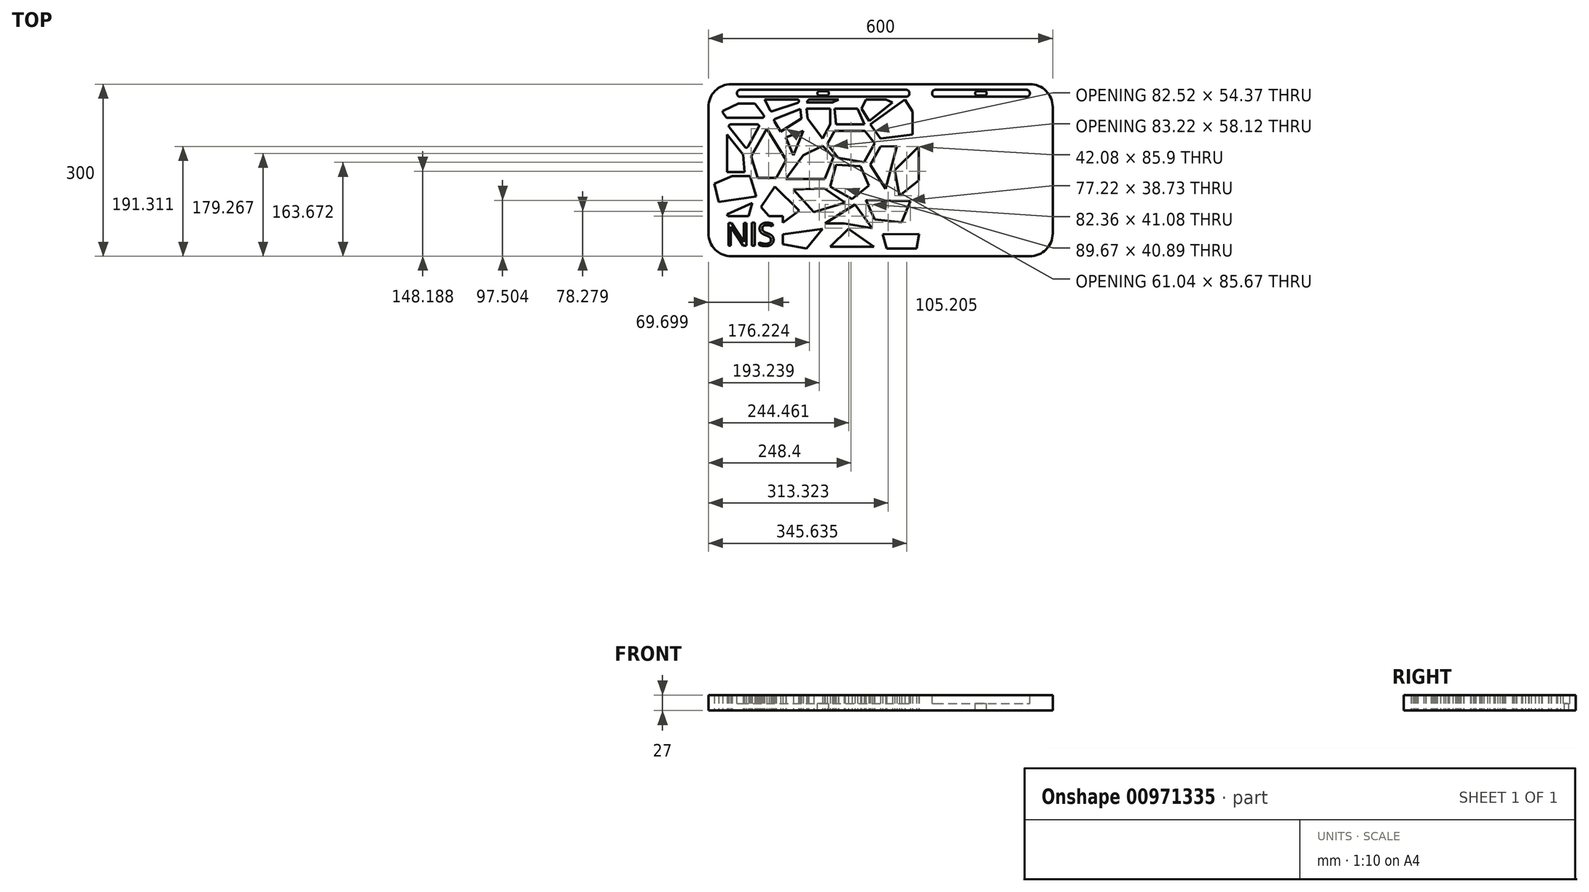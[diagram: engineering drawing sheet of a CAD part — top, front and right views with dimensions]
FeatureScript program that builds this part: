
annotation { "Feature Type Name" : "Feature", "Feature Type Description" : "" }
export const myFeature = defineFeature(function(context is Context, id is Id, definition is map)
    precondition{}
    {
        {
            var Q0;
            Q0=qCreatedBy(makeId("Top.planeOp"),FACE);
            var sketch = newSketch(context, id + "F0", { "sketchPlane" : qUnion([Q0])});
            skLineSegment(sketch, "E0.bottom", {"start": v(260, 150) * mm, "end": v(-260, 150) * mm});
            skLineSegment(sketch, "E0.top", {"start": v(260, -150) * mm, "end": v(-260, -150) * mm});
            skLineSegment(sketch, "E0.left", {"start": v(300, 110) * mm, "end": v(300, -110) * mm});
            skLineSegment(sketch, "E0.right", {"start": v(-300, 110) * mm, "end": v(-300, -110) * mm});
            skPoint(sketch, "E0.middle", {"position": v(0, 0) * mm});
            skPoint(sketch, "E1.visualSharp", {"position": v(-300, 150) * mm});
            skArc(sketch, "E1.filletArc", {"start": v(-260, 150) * mm, "mid": v(-288.28, 138.28) * mm, "end": v(-300, 110) * mm});
            skPoint(sketch, "E2.visualSharp", {"position": v(-300, -150) * mm});
            skArc(sketch, "E2.filletArc", {"start": v(-300, -110) * mm, "mid": v(-288.28, -138.28) * mm, "end": v(-260, -150) * mm});
            skPoint(sketch, "E3.visualSharp", {"position": v(300, -150) * mm});
            skArc(sketch, "E3.filletArc", {"start": v(260, -150) * mm, "mid": v(288.28, -138.28) * mm, "end": v(300, -110) * mm});
            skPoint(sketch, "E4.visualSharp", {"position": v(300, 150) * mm});
            skArc(sketch, "E4.filletArc", {"start": v(300, 110) * mm, "mid": v(288.28, 138.28) * mm, "end": v(260, 150) * mm});
            skLineSegment(sketch, "E5", {"start": v(80, 150) * mm, "end": v(80, -150) * mm, "construction": true});
            skSolve(sketch);
        }
        {
            var Q0;
            Q0=makeQuery(id+"F0.imprint","IMPRINT",FACE,{"disambiguationData":[TD([[makeQuery(id+"F0.imprint","IMPRINT",EDGE,{"derivedFrom":sQuery(id+"F0.wireOp",EDGE,"E0.bottom")}),1.0]])]});
            var sketch = newSketch(context, id + "F1", { "sketchPlane" : qUnion([Q0])});
            skLineSegment(sketch, "E6", {"start": v(-273.2, 104.35) * mm, "end": v(-247.8, 116.08) * mm});
            skLineSegment(sketch, "E7", {"start": v(-246.54, 116.36) * mm, "end": v(-221.1, 116.36) * mm});
            skLineSegment(sketch, "E8", {"start": v(-218.74, 115.22) * mm, "end": v(-203.73, 96.16) * mm});
            skLineSegment(sketch, "E9", {"start": v(-206.09, 91.3) * mm, "end": v(-266.95, 91.3) * mm});
            skLineSegment(sketch, "E10", {"start": v(-269.43, 92.61) * mm, "end": v(-274.42, 99.94) * mm});
            skLineSegment(sketch, "E11", {"start": v(-184.96, 85.23) * mm, "end": v(-173.85, 67.5) * mm});
            skLineSegment(sketch, "E12", {"start": v(-173.85, 67.5) * mm, "end": v(-137.63, 90.2) * mm});
            skLineSegment(sketch, "E13", {"start": v(-137.63, 90.2) * mm, "end": v(-140.04, 106.58) * mm});
            skLineSegment(sketch, "E14", {"start": v(-140.04, 106.58) * mm, "end": v(-183.5, 89.61) * mm});
            skLineSegment(sketch, "E15", {"start": v(-202.21, 122.97) * mm, "end": v(-192.5, 104.48) * mm});
            skLineSegment(sketch, "E16", {"start": v(-188.92, 103.02) * mm, "end": v(-144.36, 117.51) * mm});
            skLineSegment(sketch, "E17", {"start": v(-142.34, 120.89) * mm, "end": v(-142.7, 122.97) * mm});
            skLineSegment(sketch, "E18", {"start": v(-129.26, 107.06) * mm, "end": v(-126.94, 90) * mm});
            skLineSegment(sketch, "E19", {"start": v(-126.94, 90) * mm, "end": v(-101.24, 55.24) * mm});
            skLineSegment(sketch, "E20", {"start": v(-101.24, 55.24) * mm, "end": v(-87.55, 79.67) * mm});
            skLineSegment(sketch, "E21", {"start": v(-87.55, 79.67) * mm, "end": v(-87.55, 107.48) * mm});
            skLineSegment(sketch, "E22", {"start": v(-87.55, 107.48) * mm, "end": v(-129.26, 107.06) * mm});
            skLineSegment(sketch, "E23", {"start": v(-79.98, 107.06) * mm, "end": v(-77.5, 79.67) * mm});
            skLineSegment(sketch, "E24", {"start": v(-77.5, 79.67) * mm, "end": v(-27.9, 79.67) * mm});
            skLineSegment(sketch, "E25", {"start": v(-27.9, 79.67) * mm, "end": v(-39.95, 107.06) * mm});
            skLineSegment(sketch, "E26", {"start": v(-39.95, 107.06) * mm, "end": v(-79.98, 107.06) * mm});
            skLineSegment(sketch, "E27", {"start": v(-263.7, 74.8) * mm, "end": v(-236.4, 40.48) * mm});
            skLineSegment(sketch, "E28", {"start": v(-231.43, 40.88) * mm, "end": v(-212.2, 75.2) * mm});
            skLineSegment(sketch, "E29", {"start": v(-214.81, 79.67) * mm, "end": v(-261.36, 79.67) * mm});
            skLineSegment(sketch, "E30", {"start": v(-198.5, 72.1) * mm, "end": v(-225.31, 24.27) * mm});
            skLineSegment(sketch, "E31", {"start": v(-225.31, 24.27) * mm, "end": v(-214.04, -13.57) * mm});
            skLineSegment(sketch, "E32", {"start": v(-214.04, -13.57) * mm, "end": v(-181.98, -13.57) * mm});
            skLineSegment(sketch, "E33", {"start": v(-181.98, -13.57) * mm, "end": v(-164.28, 18.02) * mm});
            skLineSegment(sketch, "E34", {"start": v(-164.28, 18.02) * mm, "end": v(-198.5, 72.1) * mm});
            skLineSegment(sketch, "E35", {"start": v(-165.39, 56.97) * mm, "end": v(-151.83, 26.15) * mm});
            skLineSegment(sketch, "E36", {"start": v(-151.83, 26.15) * mm, "end": v(-134.83, 68.5) * mm});
            skLineSegment(sketch, "E37", {"start": v(-134.83, 68.5) * mm, "end": v(-165.39, 56.97) * mm});
            skLineSegment(sketch, "E38", {"start": v(-267.58, 62.27) * mm, "end": v(-239.65, 27.15) * mm});
            skLineSegment(sketch, "E39", {"start": v(-239.65, 27.15) * mm, "end": v(-236.87, -3.55) * mm});
            skLineSegment(sketch, "E40", {"start": v(-236.87, -3.55) * mm, "end": v(-267.58, -3.55) * mm});
            skLineSegment(sketch, "E41", {"start": v(-267.58, -3.55) * mm, "end": v(-267.58, 62.27) * mm});
            skLineSegment(sketch, "E42", {"start": v(-134.83, 26.2) * mm, "end": v(-165.39, -15.39) * mm});
            skLineSegment(sketch, "E43", {"start": v(-165.39, -15.39) * mm, "end": v(-97.55, -15.39) * mm});
            skLineSegment(sketch, "E44", {"start": v(-97.55, -15.39) * mm, "end": v(-82.16, 22.94) * mm});
            skLineSegment(sketch, "E45", {"start": v(-82.16, 22.94) * mm, "end": v(-101.24, 42.73) * mm});
            skLineSegment(sketch, "E46", {"start": v(-101.24, 42.73) * mm, "end": v(-134.83, 26.2) * mm});
            skLineSegment(sketch, "E47", {"start": v(-129.26, 118.32) * mm, "end": v(-83.9, 118.32) * mm});
            skLineSegment(sketch, "E48", {"start": v(-83.9, 118.32) * mm, "end": v(-73.33, 122.97) * mm});
            skLineSegment(sketch, "E49", {"start": v(-33.3, 107.06) * mm, "end": v(-19.85, 85.83) * mm});
            skLineSegment(sketch, "E50", {"start": v(-19.85, 85.83) * mm, "end": v(21, 118.32) * mm});
            skLineSegment(sketch, "E51", {"start": v(21, 118.32) * mm, "end": v(9.4, 122.97) * mm});
            skLineSegment(sketch, "E52", {"start": v(-25.38, 122.97) * mm, "end": v(-33.3, 107.06) * mm});
            skLineSegment(sketch, "E53", {"start": v(42.52, 123.2) * mm, "end": v(55.79, 102.24) * mm});
            skLineSegment(sketch, "E54", {"start": v(55.79, 102.24) * mm, "end": v(55.79, 62.27) * mm});
            skLineSegment(sketch, "E55", {"start": v(55.79, 62.27) * mm, "end": v(0, 55.24) * mm});
            skLineSegment(sketch, "E56", {"start": v(0, 55.24) * mm, "end": v(-18.07, 79.67) * mm});
            skLineSegment(sketch, "E57", {"start": v(-18.07, 79.67) * mm, "end": v(42.52, 123.2) * mm});
            skLineSegment(sketch, "E58", {"start": v(-79.98, 68.5) * mm, "end": v(-92.86, 45.51) * mm});
            skLineSegment(sketch, "E59", {"start": v(-92.86, 45.51) * mm, "end": v(-73.99, 21.8) * mm});
            skLineSegment(sketch, "E60", {"start": v(-73.99, 21.8) * mm, "end": v(-28.83, 14.13) * mm});
            skLineSegment(sketch, "E61", {"start": v(-28.83, 14.13) * mm, "end": v(-10.34, 47.12) * mm});
            skLineSegment(sketch, "E62", {"start": v(-10.34, 47.12) * mm, "end": v(-27.34, 68.5) * mm});
            skLineSegment(sketch, "E63", {"start": v(-27.34, 68.5) * mm, "end": v(-79.98, 68.5) * mm});
            skLineSegment(sketch, "E64", {"start": v(-77.5, 9.58) * mm, "end": v(-87.55, -28.5) * mm});
            skLineSegment(sketch, "E65", {"start": v(-87.55, -28.5) * mm, "end": v(-49.32, -49.92) * mm});
            skLineSegment(sketch, "E66", {"start": v(-49.32, -49.92) * mm, "end": v(-20.2, -26.75) * mm});
            skLineSegment(sketch, "E67", {"start": v(-20.2, -26.75) * mm, "end": v(-35.07, 7.05) * mm});
            skLineSegment(sketch, "E68", {"start": v(-35.07, 7.05) * mm, "end": v(-77.5, 9.58) * mm});
            skLineSegment(sketch, "E69", {"start": v(0, 41.14) * mm, "end": v(-17.69, 9.58) * mm});
            skLineSegment(sketch, "E70", {"start": v(-17.69, 9.58) * mm, "end": v(8.76, -32.2) * mm});
            skLineSegment(sketch, "E71", {"start": v(8.76, -32.2) * mm, "end": v(28.33, 41.95) * mm});
            skLineSegment(sketch, "E72", {"start": v(28.33, 41.95) * mm, "end": v(0, 41.14) * mm});
            skLineSegment(sketch, "E73", {"start": v(24.6, 0) * mm, "end": v(66.68, 41.14) * mm});
            skLineSegment(sketch, "E74", {"start": v(66.68, 41.14) * mm, "end": v(66.68, -17.98) * mm});
            skLineSegment(sketch, "E75", {"start": v(66.68, -17.98) * mm, "end": v(33, -44.76) * mm});
            skLineSegment(sketch, "E76", {"start": v(33, -44.76) * mm, "end": v(24.6, 0) * mm});
            skLineSegment(sketch, "E77", {"start": v(-289.54, -23.85) * mm, "end": v(-258.24, -10.08) * mm});
            skLineSegment(sketch, "E78", {"start": v(-258.24, -10.08) * mm, "end": v(-227.41, -10.08) * mm});
            skLineSegment(sketch, "E79", {"start": v(-227.41, -10.08) * mm, "end": v(-216.84, -45.58) * mm});
            skLineSegment(sketch, "E80", {"start": v(-216.84, -45.58) * mm, "end": v(-282.02, -55.41) * mm});
            skLineSegment(sketch, "E81", {"start": v(-282.02, -55.41) * mm, "end": v(-289.54, -23.85) * mm});
            skLineSegment(sketch, "E82", {"start": v(-184.06, -28.5) * mm, "end": v(-208.5, -64.27) * mm});
            skLineSegment(sketch, "E83", {"start": v(-208.5, -64.27) * mm, "end": v(-194.3, -80) * mm});
            skLineSegment(sketch, "E84", {"start": v(-170, -91.42) * mm, "end": v(-141.88, -70.63) * mm});
            skLineSegment(sketch, "E85", {"start": v(-141.88, -70.63) * mm, "end": v(-184.06, -28.5) * mm});
            skLineSegment(sketch, "E86", {"start": v(-151.6, -33.6) * mm, "end": v(-97.67, -32.05) * mm});
            skLineSegment(sketch, "E87", {"start": v(-97.67, -32.05) * mm, "end": v(-61.93, -56.83) * mm});
            skLineSegment(sketch, "E88", {"start": v(-61.93, -56.83) * mm, "end": v(-116.02, -72.94) * mm});
            skLineSegment(sketch, "E89", {"start": v(-116.02, -72.94) * mm, "end": v(-151.6, -33.6) * mm});
            skLineSegment(sketch, "E90", {"start": v(-25.29, -52.36) * mm, "end": v(-10.53, -85.91) * mm});
            skLineSegment(sketch, "E91", {"start": v(-10.53, -85.91) * mm, "end": v(36.97, -91.08) * mm});
            skLineSegment(sketch, "E92", {"start": v(36.97, -91.08) * mm, "end": v(51.93, -53.82) * mm});
            skLineSegment(sketch, "E93", {"start": v(51.93, -53.82) * mm, "end": v(-25.29, -52.36) * mm});
            skLineSegment(sketch, "E94", {"start": v(-267.58, -76.66) * mm, "end": v(-223.88, -57.44) * mm});
            skLineSegment(sketch, "E95", {"start": v(-223.88, -57.44) * mm, "end": v(-229.83, -80) * mm});
            skLineSegment(sketch, "E96", {"start": v(-265.98, -80) * mm, "end": v(-267.58, -76.66) * mm});
            skLineSegment(sketch, "E97", {"start": v(-170, -128.9) * mm, "end": v(-129.26, -136.9) * mm});
            skLineSegment(sketch, "E98", {"start": v(-129.26, -136.9) * mm, "end": v(-101.24, -102.36) * mm});
            skLineSegment(sketch, "E99", {"start": v(-101.24, -102.36) * mm, "end": v(-170, -111.76) * mm});
            skLineSegment(sketch, "E100", {"start": v(-63.44, -92.67) * mm, "end": v(-96.72, -92.67) * mm});
            skLineSegment(sketch, "E101", {"start": v(-96.72, -92.67) * mm, "end": v(-44.74, -59.76) * mm});
            skLineSegment(sketch, "E102", {"start": v(-44.74, -59.76) * mm, "end": v(-14.36, -100.84) * mm});
            skLineSegment(sketch, "E103", {"start": v(-14.36, -100.84) * mm, "end": v(-63.44, -92.67) * mm});
            skLineSegment(sketch, "E104", {"start": v(-87.55, -133.1) * mm, "end": v(-11.62, -133.1) * mm});
            skLineSegment(sketch, "E105", {"start": v(-11.62, -133.1) * mm, "end": v(-56.1, -102.28) * mm});
            skLineSegment(sketch, "E106", {"start": v(-56.1, -102.28) * mm, "end": v(-87.55, -133.1) * mm});
            skLineSegment(sketch, "E107", {"start": v(3.55, -112.05) * mm, "end": v(10.78, -136.33) * mm});
            skLineSegment(sketch, "E108", {"start": v(10.78, -136.33) * mm, "end": v(62.52, -136.33) * mm});
            skLineSegment(sketch, "E109", {"start": v(62.52, -136.33) * mm, "end": v(67.47, -111.19) * mm});
            skLineSegment(sketch, "E110", {"start": v(67.47, -111.19) * mm, "end": v(3.55, -112.05) * mm});
            skPoint(sketch, "E111.visualSharp", {"position": v(-276.4, 102.86) * mm});
            skArc(sketch, "E111.filletArc", {"start": v(-273.2, 104.35) * mm, "mid": v(-274.83, 102.42) * mm, "end": v(-274.42, 99.94) * mm});
            skPoint(sketch, "E112.visualSharp", {"position": v(-268.54, 91.3) * mm});
            skArc(sketch, "E112.filletArc", {"start": v(-269.43, 92.61) * mm, "mid": v(-268.36, 91.65) * mm, "end": v(-266.95, 91.3) * mm});
            skPoint(sketch, "E113.visualSharp", {"position": v(-199.9, 91.3) * mm});
            skArc(sketch, "E113.filletArc", {"start": v(-206.09, 91.3) * mm, "mid": v(-203.39, 93) * mm, "end": v(-203.73, 96.16) * mm});
            skPoint(sketch, "E114.visualSharp", {"position": v(-219.64, 116.36) * mm});
            skArc(sketch, "E114.filletArc", {"start": v(-218.74, 115.22) * mm, "mid": v(-219.79, 116.06) * mm, "end": v(-221.1, 116.36) * mm});
            skPoint(sketch, "E115.visualSharp", {"position": v(-247.2, 116.36) * mm});
            skArc(sketch, "E115.filletArc", {"start": v(-246.54, 116.36) * mm, "mid": v(-247.18, 116.29) * mm, "end": v(-247.8, 116.08) * mm});
            skPoint(sketch, "E116.visualSharp", {"position": v(-267.58, 79.67) * mm});
            skArc(sketch, "E116.filletArc", {"start": v(-261.36, 79.67) * mm, "mid": v(-264.06, 77.98) * mm, "end": v(-263.7, 74.8) * mm});
            skPoint(sketch, "E117.visualSharp", {"position": v(-233.62, 36.98) * mm});
            skArc(sketch, "E117.filletArc", {"start": v(-236.4, 40.48) * mm, "mid": v(-233.8, 39.36) * mm, "end": v(-231.43, 40.88) * mm});
            skPoint(sketch, "E118.visualSharp", {"position": v(-209.7, 79.67) * mm});
            skArc(sketch, "E118.filletArc", {"start": v(-212.2, 75.2) * mm, "mid": v(-212.23, 78.2) * mm, "end": v(-214.81, 79.67) * mm});
            skPoint(sketch, "E119.visualSharp", {"position": v(-191.33, 102.24) * mm});
            skArc(sketch, "E119.filletArc", {"start": v(-192.5, 104.48) * mm, "mid": v(-190.98, 103.1) * mm, "end": v(-188.92, 103.02) * mm});
            skPoint(sketch, "E120.visualSharp", {"position": v(-141.88, 118.32) * mm});
            skArc(sketch, "E120.filletArc", {"start": v(-144.36, 117.51) * mm, "mid": v(-142.72, 118.82) * mm, "end": v(-142.34, 120.89) * mm});
            skPoint(sketch, "E121.visualSharp", {"position": v(-186.88, 88.3) * mm});
            skArc(sketch, "E121.filletArc", {"start": v(-183.5, 89.61) * mm, "mid": v(-185.26, 87.76) * mm, "end": v(-184.96, 85.23) * mm});
            skLineSegment(sketch, "E122.bottom", {"start": v(-265.98, -80) * mm, "end": v(-229.83, -80) * mm});
            skLineSegment(sketch, "E122.right", {"start": v(-170, -80) * mm, "end": v(-170, -91.42) * mm});
            skText(sketch, "E123", { "text": "N S", "fontName": "OpenSans-Regular.ttf"});
            skLineSegment(sketch, "E124.trimOffspring", {"start": v(-170, -111.76) * mm, "end": v(-170, -128.9) * mm});
            skLineSegment(sketch, "E125.trimOffspring", {"start": v(-194.3, -80) * mm, "end": v(-170, -80) * mm});
            skLineSegment(sketch, "E126", {"start": v(-224, -91.74) * mm, "end": v(-219.14, -91.74) * mm});
            skLineSegment(sketch, "E127.top", {"start": v(-224, -131.74) * mm, "end": v(-219.14, -131.74) * mm});
            skLineSegment(sketch, "E127.left", {"start": v(-224, -91.74) * mm, "end": v(-224, -131.74) * mm});
            skLineSegment(sketch, "E127.right", {"start": v(-219.14, -91.74) * mm, "end": v(-219.14, -131.74) * mm});
            skLineSegment(sketch, "E128.top", {"start": v(-202.21, 122.97) * mm, "end": v(-142.7, 122.97) * mm});
            skLineSegment(sketch, "E129.trimOffspring", {"start": v(-125.42, 122.97) * mm, "end": v(-129.26, 118.32) * mm});
            skLineSegment(sketch, "E130.trimOffspring", {"start": v(42.2, 122.97) * mm, "end": v(42.66, 122.97) * mm});
            skLineSegment(sketch, "E131.trimOffspring", {"start": v(-25.38, 122.97) * mm, "end": v(9.4, 122.97) * mm});
            skLineSegment(sketch, "E132.trimOffspring", {"start": v(-125.42, 122.97) * mm, "end": v(-73.33, 122.97) * mm});
            const initialGuessF1  = {"E123": [-0.27052, -0.13174, 1, 0, 0.04]};
            skSetInitialGuess(sketch, initialGuessF1);
            skSolve(sketch);
        }
        {
            var Q0;
            Q0 = qSketchRegion(id + "F0", true);
            extrude(context, id + "F2", {"entities" : qUnion([Q0]), "depth" : 27 * mm, "offsetDistance" : 25 * mm});
        }
        {
            var Q0;
            Q0 = qSketchRegion(id + "F1", true);
            extrude(context, id + "F3", {"entities" : qUnion([Q0]), "operationType" : NewBodyOperationType.REMOVE, "depth" : 27 * mm, "offsetDistance" : 25 * mm});
        }
        {
            var Q0;
            Q0=makeQuery(id+"F2.opExtrude","CAP_FACE",FACE,{"disambiguationData":[OSD([sQuery(id+"F0.wireOp",EDGE,"E0.bottom"),sQuery(id+"F0.wireOp",EDGE,"E0.top"),sQuery(id+"F0.wireOp",EDGE,"E0.left"),sQuery(id+"F0.wireOp",EDGE,"E0.right"),sQuery(id+"F0.wireOp",EDGE,"E1.filletArc"),sQuery(id+"F0.wireOp",EDGE,"E2.filletArc"),sQuery(id+"F0.wireOp",EDGE,"E3.filletArc"),sQuery(id+"F0.wireOp",EDGE,"E4.filletArc")])],"isStart":false});
            var sketch = newSketch(context, id + "F4", { "sketchPlane" : qUnion([Q0])});
            skLineSegment(sketch, "E133.bottom", {"start": v(-245, 140) * mm, "end": v(45, 140) * mm});
            skLineSegment(sketch, "E133.top", {"start": v(-245, 128) * mm, "end": v(45, 128) * mm});
            skLineSegment(sketch, "E133.left", {"start": v(-250, 135) * mm, "end": v(-250, 133) * mm});
            skLineSegment(sketch, "E133.right", {"start": v(50, 135) * mm, "end": v(50, 133) * mm});
            skLineSegment(sketch, "E134.bottom", {"start": v(95, 140) * mm, "end": v(255, 140) * mm});
            skLineSegment(sketch, "E134.top", {"start": v(95, 128) * mm, "end": v(255, 128) * mm});
            skLineSegment(sketch, "E134.left", {"start": v(90, 135) * mm, "end": v(90, 133) * mm});
            skLineSegment(sketch, "E134.right", {"start": v(260, 135) * mm, "end": v(260, 133) * mm});
            skPoint(sketch, "E135.visualSharp", {"position": v(-250, 140) * mm});
            skArc(sketch, "E135.filletArc", {"start": v(-245, 140) * mm, "mid": v(-248.54, 138.54) * mm, "end": v(-250, 135) * mm});
            skPoint(sketch, "E136.visualSharp", {"position": v(-250, 128) * mm});
            skArc(sketch, "E136.filletArc", {"start": v(-250, 133) * mm, "mid": v(-248.54, 129.46) * mm, "end": v(-245, 128) * mm});
            skPoint(sketch, "E137.visualSharp", {"position": v(50, 128) * mm});
            skArc(sketch, "E137.filletArc", {"start": v(45, 128) * mm, "mid": v(48.54, 129.46) * mm, "end": v(50, 133) * mm});
            skPoint(sketch, "E138.visualSharp", {"position": v(50, 140) * mm});
            skArc(sketch, "E138.filletArc", {"start": v(50, 135) * mm, "mid": v(48.54, 138.54) * mm, "end": v(45, 140) * mm});
            skPoint(sketch, "E139.visualSharp", {"position": v(90, 140) * mm});
            skArc(sketch, "E139.filletArc", {"start": v(95, 140) * mm, "mid": v(91.46, 138.54) * mm, "end": v(90, 135) * mm});
            skPoint(sketch, "E140.visualSharp", {"position": v(90, 128) * mm});
            skArc(sketch, "E140.filletArc", {"start": v(90, 133) * mm, "mid": v(91.46, 129.46) * mm, "end": v(95, 128) * mm});
            skPoint(sketch, "E141.visualSharp", {"position": v(260, 128) * mm});
            skArc(sketch, "E141.filletArc", {"start": v(255, 128) * mm, "mid": v(258.54, 129.46) * mm, "end": v(260, 133) * mm});
            skPoint(sketch, "E142.visualSharp", {"position": v(260, 140) * mm});
            skArc(sketch, "E142.filletArc", {"start": v(260, 135) * mm, "mid": v(258.54, 138.54) * mm, "end": v(255, 140) * mm});
            skSolve(sketch);
        }
        {
            var Q0;
            Q0=makeQuery(id+"F4.imprint","IMPRINT",FACE,{"disambiguationData":[TD([[makeQuery(id+"F4.imprint","IMPRINT",EDGE,{"derivedFrom":sQuery(id+"F4.wireOp",EDGE,"E133.bottom")}),-1.0]])]});
            var Q1;
            Q1=makeQuery(id+"F4.imprint","IMPRINT",FACE,{"disambiguationData":[TD([[makeQuery(id+"F4.imprint","IMPRINT",EDGE,{"derivedFrom":sQuery(id+"F4.wireOp",EDGE,"E134.bottom")}),-1.0]])]});
            extrude(context, id + "F5", {"entities" : qUnion([Q0, Q1]), "operationType" : NewBodyOperationType.REMOVE, "oppositeDirection" : true, "depth" : 15 * mm, "offsetDistance" : 25 * mm});
        }
        {
            var Q0;
            Q0=makeQuery(id+"F5.boolean.opBoolean","COPY",FACE,{"derivedFrom":makeQuery(id+"F5.opExtrude","CAP_FACE",FACE,{"disambiguationData":[OSD([sQuery(id+"F4.wireOp",EDGE,"E133.bottom"),sQuery(id+"F4.wireOp",EDGE,"E133.top"),sQuery(id+"F4.wireOp",EDGE,"E133.left"),sQuery(id+"F4.wireOp",EDGE,"E133.right"),sQuery(id+"F4.wireOp",EDGE,"E135.filletArc"),sQuery(id+"F4.wireOp",EDGE,"E136.filletArc"),sQuery(id+"F4.wireOp",EDGE,"E137.filletArc"),sQuery(id+"F4.wireOp",EDGE,"E138.filletArc")])],"isStart":false})});
            var sketch = newSketch(context, id + "F6", { "sketchPlane" : qUnion([Q0])});
            skLineSegment(sketch, "E143.bottom", {"start": v(-94, 130) * mm, "end": v(-106, 130) * mm});
            skLineSegment(sketch, "E143.top", {"start": v(-94, 138) * mm, "end": v(-106, 138) * mm});
            skLineSegment(sketch, "E143.left", {"start": v(-90, 134) * mm, "end": v(-90, 134) * mm});
            skLineSegment(sketch, "E143.right", {"start": v(-110, 134) * mm, "end": v(-110, 134) * mm});
            skPoint(sketch, "E143.middle", {"position": v(-100, 134) * mm});
            skPoint(sketch, "E144.visualSharp", {"position": v(-110, 138) * mm});
            skArc(sketch, "E144.filletArc", {"start": v(-106, 138) * mm, "mid": v(-108.83, 136.83) * mm, "end": v(-110, 134) * mm});
            skPoint(sketch, "E145.visualSharp", {"position": v(-110, 130) * mm});
            skArc(sketch, "E145.filletArc", {"start": v(-110, 134) * mm, "mid": v(-108.83, 131.17) * mm, "end": v(-106, 130) * mm});
            skPoint(sketch, "E146.visualSharp", {"position": v(-90, 130) * mm});
            skArc(sketch, "E146.filletArc", {"start": v(-94, 130) * mm, "mid": v(-91.17, 131.17) * mm, "end": v(-90, 134) * mm});
            skPoint(sketch, "E147.visualSharp", {"position": v(-90, 138) * mm});
            skArc(sketch, "E147.filletArc", {"start": v(-90, 134) * mm, "mid": v(-91.17, 136.83) * mm, "end": v(-94, 138) * mm});
            skLineSegment(sketch, "E148.bottom", {"start": v(181, 130) * mm, "end": v(169, 130) * mm});
            skLineSegment(sketch, "E148.top", {"start": v(181, 138) * mm, "end": v(169, 138) * mm});
            skLineSegment(sketch, "E148.left", {"start": v(185, 134) * mm, "end": v(185, 134) * mm});
            skLineSegment(sketch, "E148.right", {"start": v(165, 134) * mm, "end": v(165, 134) * mm});
            skPoint(sketch, "E148.middle", {"position": v(175, 134) * mm});
            skPoint(sketch, "E149.visualSharp", {"position": v(165, 138) * mm});
            skArc(sketch, "E149.filletArc", {"start": v(169, 138) * mm, "mid": v(166.17, 136.83) * mm, "end": v(165, 134) * mm});
            skPoint(sketch, "E150.visualSharp", {"position": v(165, 130) * mm});
            skArc(sketch, "E150.filletArc", {"start": v(165, 134) * mm, "mid": v(166.17, 131.17) * mm, "end": v(169, 130) * mm});
            skPoint(sketch, "E151.visualSharp", {"position": v(185, 130) * mm});
            skArc(sketch, "E151.filletArc", {"start": v(181, 130) * mm, "mid": v(183.83, 131.17) * mm, "end": v(185, 134) * mm});
            skPoint(sketch, "E152.visualSharp", {"position": v(185, 138) * mm});
            skArc(sketch, "E152.filletArc", {"start": v(185, 134) * mm, "mid": v(183.83, 136.83) * mm, "end": v(181, 138) * mm});
            skSolve(sketch);
        }
        {
            var Q0;
            Q0=makeQuery(id+"F6.imprint","IMPRINT",FACE,{"disambiguationData":[TD([[makeQuery(id+"F6.imprint","IMPRINT",EDGE,{"derivedFrom":sQuery(id+"F6.wireOp",EDGE,"E143.bottom")}),-1.0]])]});
            var Q1;
            Q1=makeQuery(id+"F6.imprint","IMPRINT",FACE,{"disambiguationData":[TD([[makeQuery(id+"F6.imprint","IMPRINT",EDGE,{"derivedFrom":sQuery(id+"F6.wireOp",EDGE,"E148.bottom")}),-1.0]])]});
            extrude(context, id + "F7", {"entities" : qUnion([Q0, Q1]), "operationType" : NewBodyOperationType.REMOVE, "oppositeDirection" : true, "depth" : 25 * mm, "offsetDistance" : 25 * mm});
        }
    });
